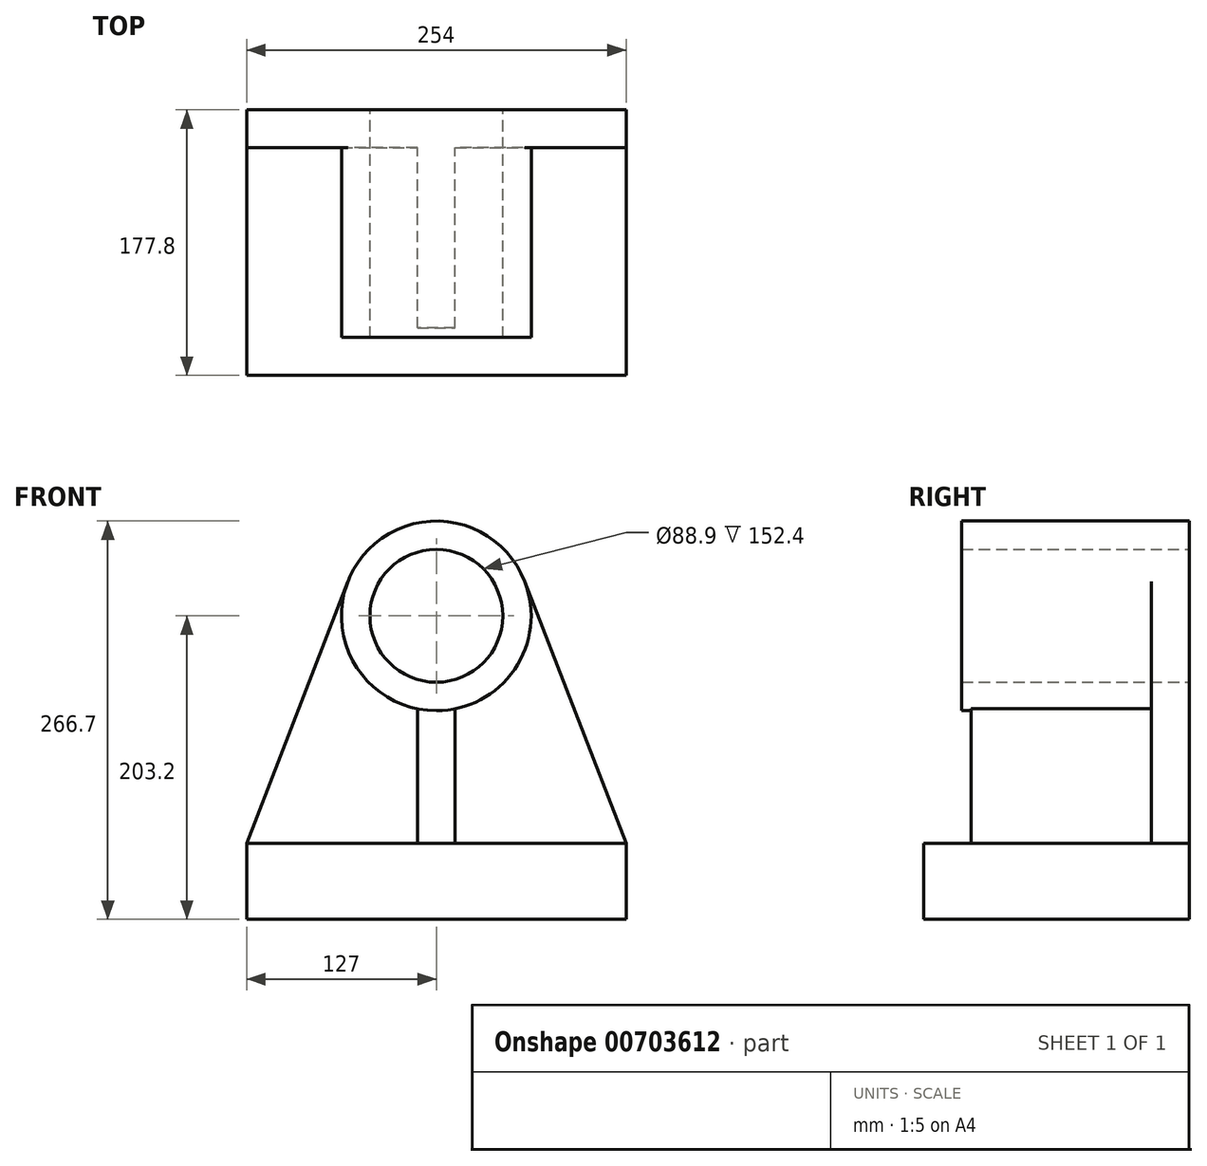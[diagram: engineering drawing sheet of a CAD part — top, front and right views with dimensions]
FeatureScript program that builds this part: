
annotation { "Feature Type Name" : "Feature", "Feature Type Description" : "" }
export const myFeature = defineFeature(function(context is Context, id is Id, definition is map)
    precondition{}
    {
        {
            var Q0;
            Q0=qCreatedBy(makeId("Front.planeOp"),FACE);
            var sketch = newSketch(context, id + "F0", { "sketchPlane" : qUnion([Q0])});
            skLineSegment(sketch, "E0", {"start": v(0, 0) * mm, "end": v(0, 50.8) * mm});
            skLineSegment(sketch, "E1", {"start": v(0, 50.8) * mm, "end": v(67.77, 226.1) * mm});
            skLineSegment(sketch, "E2", {"start": v(0, 0) * mm, "end": v(254, 0) * mm});
            skLineSegment(sketch, "E3", {"start": v(254, 0) * mm, "end": v(254, 50.8) * mm});
            skLineSegment(sketch, "E4", {"start": v(254, 50.8) * mm, "end": v(186.23, 226.1) * mm});
            skArc(sketch, "E5", {"start": v(186.23, 226.1) * mm, "mid": v(127, 266.7) * mm, "end": v(67.77, 226.1) * mm});
            skLineSegment(sketch, "E6", {"start": v(127, 0) * mm, "end": v(127, 375.67) * mm, "construction": true});
            skCircle(sketch, "E7", {"center": v(127, 203.2) * mm, "radius": 44.45 * mm});
            skSolve(sketch);
        }
        {
            var Q0;
            Q0 = qSketchRegion(id + "F0", true);
            extrude(context, id + "F1", {"entities" : qUnion([Q0]), "depth" : 25.4 * mm, "offsetDistance" : 25.4 * mm});
        }
        {
            var Q0;
            Q0=makeQuery(id+"F1.opExtrude","CAP_FACE",FACE,{"disambiguationData":[OSD([sQuery(id+"F0.wireOp",EDGE,"E0"),sQuery(id+"F0.wireOp",EDGE,"E1"),sQuery(id+"F0.wireOp",EDGE,"E2"),sQuery(id+"F0.wireOp",EDGE,"E3"),sQuery(id+"F0.wireOp",EDGE,"E4"),sQuery(id+"F0.wireOp",EDGE,"E5"),sQuery(id+"F0.wireOp",EDGE,"E7")])],"isStart":false});
            var sketch = newSketch(context, id + "F2", { "sketchPlane" : qUnion([Q0])});
            skCircle(sketch, "E8", {"center": v(127, 203.2) * mm, "radius": 63.5 * mm});
            skCircle(sketch, "E9", {"center": v(127, 203.2) * mm, "radius": 44.45 * mm});
            skSolve(sketch);
        }
        {
            var Q0;
            Q0 = qSketchRegion(id + "F2", true);
            extrude(context, id + "F3", {"entities" : qUnion([Q0]), "operationType" : NewBodyOperationType.ADD, "depth" : 127 * mm, "offsetDistance" : 25.4 * mm});
        }
        {
            var Q0;
            Q0=makeQuery(id+"F1.opExtrude","CAP_FACE",FACE,{"disambiguationData":[OSD([sQuery(id+"F0.wireOp",EDGE,"E0"),sQuery(id+"F0.wireOp",EDGE,"E1"),sQuery(id+"F0.wireOp",EDGE,"E2"),sQuery(id+"F0.wireOp",EDGE,"E3"),sQuery(id+"F0.wireOp",EDGE,"E4"),sQuery(id+"F0.wireOp",EDGE,"E5"),sQuery(id+"F0.wireOp",EDGE,"E7")])],"isStart":false});
            var sketch = newSketch(context, id + "F4", { "sketchPlane" : qUnion([Q0])});
            skLineSegment(sketch, "E10", {"start": v(0, 50.8) * mm, "end": v(0, 0) * mm});
            skLineSegment(sketch, "E11", {"start": v(0, 0) * mm, "end": v(254, 0) * mm});
            skLineSegment(sketch, "E12", {"start": v(254, 0) * mm, "end": v(254, 50.8) * mm});
            skLineSegment(sketch, "E13", {"start": v(254, 50.8) * mm, "end": v(0, 50.8) * mm});
            skSolve(sketch);
        }
        {
            var Q0;
            Q0 = qSketchRegion(id + "F4", true);
            extrude(context, id + "F5", {"entities" : qUnion([Q0]), "operationType" : NewBodyOperationType.ADD, "depth" : 152.4 * mm, "offsetDistance" : 25.4 * mm});
        }
        {
            var Q0;
            Q0=makeQuery(id+"F1.opExtrude","CAP_FACE",FACE,{"disambiguationData":[OSD([sQuery(id+"F0.wireOp",EDGE,"E0"),sQuery(id+"F0.wireOp",EDGE,"E1"),sQuery(id+"F0.wireOp",EDGE,"E2"),sQuery(id+"F0.wireOp",EDGE,"E3"),sQuery(id+"F0.wireOp",EDGE,"E4"),sQuery(id+"F0.wireOp",EDGE,"E5"),sQuery(id+"F0.wireOp",EDGE,"E7")])],"isStart":false});
            var sketch = newSketch(context, id + "F6", { "sketchPlane" : qUnion([Q0])});
            skLineSegment(sketch, "E14", {"start": v(114.3, 140.98) * mm, "end": v(114.3, 50.8) * mm});
            skLineSegment(sketch, "E15", {"start": v(114.3, 50.8) * mm, "end": v(139.7, 50.8) * mm});
            skLineSegment(sketch, "E16", {"start": v(139.7, 50.8) * mm, "end": v(139.7, 140.98) * mm});
            skLineSegment(sketch, "E17", {"start": v(127, 50.8) * mm, "end": v(127, 296.45) * mm, "construction": true});
            skCircle(sketch, "E18", {"center": v(127, 203.2) * mm, "radius": 63.5 * mm});
            skSolve(sketch);
        }
        {
            var Q0;
            {var subQ0=sQuery(id+"F6.wireOp",EDGE,"E14");Q0=makeQuery(id+"F6.imprint","IMPRINT",FACE,{"disambiguationData":[TD([[makeQuery(id+"F6.imprint","IMPRINT",EDGE,{"derivedFrom":subQ0}),1.0]])]});}
            extrude(context, id + "F7", {"entities" : qUnion([Q0]), "operationType" : NewBodyOperationType.ADD, "depth" : 120.65 * mm, "offsetDistance" : 25.4 * mm});
        }
        {
            var Q0;
            Q0=makeQuery(id+"F3.opExtrude","CAP_FACE",FACE,{"disambiguationData":[OSD([sQuery(id+"F2.wireOp",EDGE,"E8"),sQuery(id+"F2.wireOp",EDGE,"E9")])],"isStart":false});
            var sketch = newSketch(context, id + "F8", { "sketchPlane" : qUnion([Q0])});
            skCircle(sketch, "E19.0", {"center": v(127, 203.2) * mm, "radius": 44.45 * mm});
            skSolve(sketch);
        }
        {
            var Q0;
            Q0 = qSketchRegion(id + "F8", true);
            extrude(context, id + "F9", {"entities" : qUnion([Q0]), "operationType" : NewBodyOperationType.REMOVE, "endBound" : BoundingType.THROUGH_ALL, "oppositeDirection" : true, "depth" : 25.4 * mm, "offsetDistance" : 25.4 * mm});
        }
    });
